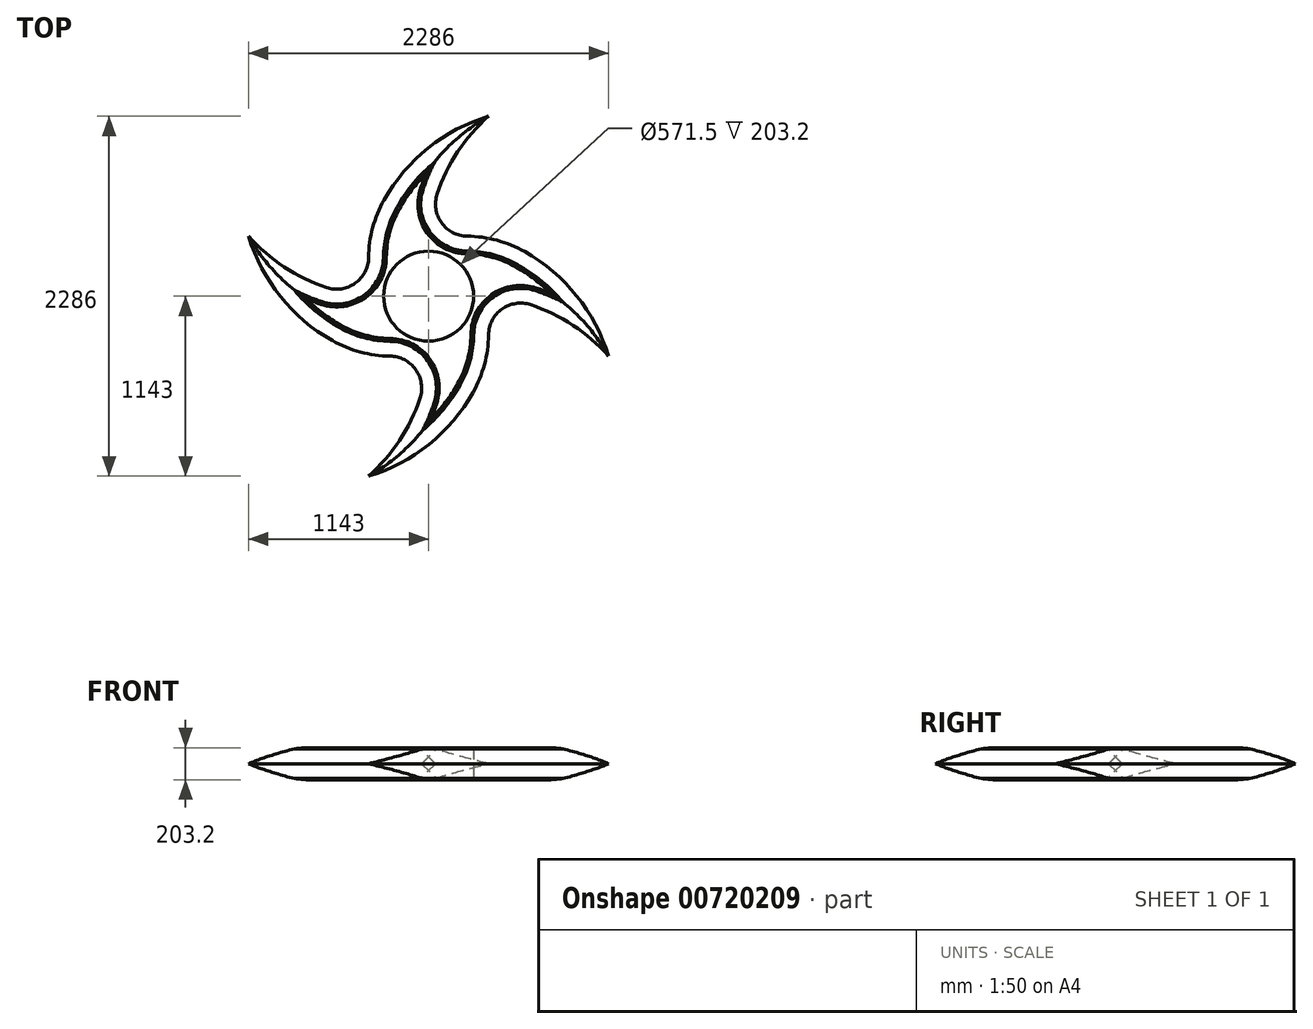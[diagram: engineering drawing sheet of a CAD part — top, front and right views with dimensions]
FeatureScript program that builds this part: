
annotation { "Feature Type Name" : "Feature", "Feature Type Description" : "" }
export const myFeature = defineFeature(function(context is Context, id is Id, definition is map)
    precondition{}
    {
        {
            var Q0;
            Q0=qCreatedBy(makeId("Top.planeOp"),FACE);
            var sketch = newSketch(context, id + "F0", { "sketchPlane" : qUnion([Q0])});
            skCircle(sketch, "E0", {"center": v(0, 0) * mm, "radius": 292.1 * mm});
            skCircle(sketch, "E1", {"center": v(0, 0) * mm, "radius": 381 * mm});
            skLineSegment(sketch, "E2", {"start": v(0, 0) * mm, "end": v(0, 381) * mm});
            skLineSegment(sketch, "E3", {"start": v(0, 381) * mm, "end": v(-381, 381) * mm});
            skLineSegment(sketch, "E4", {"start": v(-381, 381) * mm, "end": v(-381, -381) * mm});
            skLineSegment(sketch, "E5", {"start": v(-381, -381) * mm, "end": v(381, -381) * mm});
            skLineSegment(sketch, "E6", {"start": v(381, -381) * mm, "end": v(381, 381) * mm});
            skLineSegment(sketch, "E7", {"start": v(381, 381) * mm, "end": v(0, 381) * mm});
            skArc(sketch, "E8", {"start": v(381, 1143) * mm, "mid": v(-95.44, 857.44) * mm, "end": v(-381, 381) * mm});
            skArc(sketch, "E9", {"start": v(381, 1143) * mm, "mid": v(116.85, 798.82) * mm, "end": v(0, 381) * mm});
            skArc(sketch, "E10", {"start": v(-1143, 381) * mm, "mid": v(-857.44, -95.44) * mm, "end": v(-381, -381) * mm});
            skArc(sketch, "E11", {"start": v(-1143, 381) * mm, "mid": v(-798.82, 116.85) * mm, "end": v(-381, 0) * mm});
            skArc(sketch, "E12", {"start": v(-381, -1143) * mm, "mid": v(95.44, -857.44) * mm, "end": v(381, -381) * mm});
            skArc(sketch, "E13", {"start": v(-381, -1143) * mm, "mid": v(-116.85, -798.82) * mm, "end": v(0, -381) * mm});
            skArc(sketch, "E14", {"start": v(1143, -381) * mm, "mid": v(857.44, 95.44) * mm, "end": v(381, 381) * mm});
            skArc(sketch, "E15", {"start": v(1143, -381) * mm, "mid": v(798.82, -116.85) * mm, "end": v(381, 0) * mm});
            skCircle(sketch, "E16", {"center": v(0, 0) * mm, "radius": 285.75 * mm});
            skSolve(sketch);
        }
        {
            var Q0;
            {var subQ0=sQuery(id+"F0.wireOp",EDGE,"E12");Q0=makeQuery(id+"F0.imprint","IMPRINT",FACE,{"disambiguationData":[TD([[makeQuery(id+"F0.imprint","IMPRINT",EDGE,{"derivedFrom":subQ0}),1.0]])]});}
            var Q1;
            {var subQ0=sQuery(id+"F0.wireOp",EDGE,"E10");Q1=makeQuery(id+"F0.imprint","IMPRINT",FACE,{"disambiguationData":[TD([[makeQuery(id+"F0.imprint","IMPRINT",EDGE,{"derivedFrom":subQ0}),1.0]])]});}
            var Q2;
            Q2=makeQuery(id+"F0.imprint","IMPRINT",FACE,{"disambiguationData":[TD([[makeQuery(id+"F0.imprint","IMPRINT",EDGE,{"derivedFrom":sQuery(id+"F0.wireOp",EDGE,"E3")}),-1.0]])]});
            var Q3;
            {var subQ0=sQuery(id+"F0.wireOp",EDGE,"E14");Q3=makeQuery(id+"F0.imprint","IMPRINT",FACE,{"disambiguationData":[TD([[makeQuery(id+"F0.imprint","IMPRINT",EDGE,{"derivedFrom":subQ0}),1.0]])]});}
            var Q4;
            {var subQ0=sQuery(id+"F0.wireOp",EDGE,"E7");Q4=makeQuery(id+"F0.imprint","IMPRINT",FACE,{"disambiguationData":[TD([[makeQuery(id+"F0.imprint","IMPRINT",EDGE,{"derivedFrom":subQ0}),1.0]])]});}
            var Q5;
            {var subQ0=sQuery(id+"F0.wireOp",EDGE,"E3");Q5=makeQuery(id+"F0.imprint","IMPRINT",FACE,{"disambiguationData":[TD([[makeQuery(id+"F0.imprint","IMPRINT",EDGE,{"derivedFrom":subQ0}),1.0]])]});}
            var Q6;
            Q6=makeQuery(id+"F0.imprint","IMPRINT",FACE,{"disambiguationData":[TD([[makeQuery(id+"F0.imprint","IMPRINT",EDGE,{"derivedFrom":sQuery(id+"F0.wireOp",EDGE,"E0")}),-1.0]])]});
            var Q7;
            {var subQ0=sQuery(id+"F0.wireOp",EDGE,"E4");var subQ1=sQuery(id+"F0.wireOp",EDGE,"E1");var subQ2=makeQuery(id+"F0.imprint","INTERSECT",VERTEX,{"derivedFrom":[subQ1,subQ0,sQuery(id+"F0.wireOp",EDGE,"E11")]});Q7=makeQuery(id+"F0.imprint","IMPRINT",FACE,{"disambiguationData":[TD([[makeQuery(id+"F0.imprint","IMPRINT",EDGE,{"disambiguationData":[TD([[subQ2,-1.0]])],"derivedFrom":subQ1}),-1.0]])]});}
            var Q8;
            {var subQ0=sQuery(id+"F0.wireOp",EDGE,"E5");var subQ1=sQuery(id+"F0.wireOp",EDGE,"E1");var subQ2=makeQuery(id+"F0.imprint","INTERSECT",VERTEX,{"derivedFrom":[subQ1,subQ0,sQuery(id+"F0.wireOp",EDGE,"E13")]});Q8=makeQuery(id+"F0.imprint","IMPRINT",FACE,{"disambiguationData":[TD([[makeQuery(id+"F0.imprint","IMPRINT",EDGE,{"disambiguationData":[TD([[subQ2,-1.0]])],"derivedFrom":subQ1}),-1.0]])]});}
            var Q9;
            Q9=makeQuery(id+"F0.imprint","IMPRINT",FACE,{"disambiguationData":[TD([[makeQuery(id+"F0.imprint","IMPRINT",EDGE,{"derivedFrom":sQuery(id+"F0.wireOp",EDGE,"E0")}),1.0]])]});
            extrude(context, id + "F1", {"entities" : qUnion([Q0, Q1, Q2, Q3, Q4, Q5, Q6, Q7, Q8, Q9]), "depth" : 203.2 * mm, "offsetDistance" : 25.4 * mm});
        }
        {
            var Q0;
            Q0=makeQuery(id+"F1.opExtrude","SWEPT_EDGE",EDGE,{"disambiguationData":[OSD([sQuery(id+"F0.wireOp",EDGE,"E6"),sQuery(id+"F0.wireOp",EDGE,"E7"),sQuery(id+"F0.wireOp",EDGE,"E14")])]});
            var Q1;
            Q1=makeQuery(id+"F1.opExtrude","SWEPT_EDGE",EDGE,{"disambiguationData":[OSD([sQuery(id+"F0.wireOp",EDGE,"E3"),sQuery(id+"F0.wireOp",EDGE,"E4"),sQuery(id+"F0.wireOp",EDGE,"E8")])]});
            var Q2;
            Q2=makeQuery(id+"F1.opExtrude","SWEPT_EDGE",EDGE,{"disambiguationData":[OSD([sQuery(id+"F0.wireOp",EDGE,"E4"),sQuery(id+"F0.wireOp",EDGE,"E5"),sQuery(id+"F0.wireOp",EDGE,"E10")])]});
            var Q3;
            Q3=makeQuery(id+"F1.opExtrude","SWEPT_EDGE",EDGE,{"disambiguationData":[OSD([sQuery(id+"F0.wireOp",EDGE,"E5"),sQuery(id+"F0.wireOp",EDGE,"E6"),sQuery(id+"F0.wireOp",EDGE,"E12")])]});
            fillet(context, id + "F2", {"entities" : qUnion([Q0, Q1, Q2, Q3]), "radius" : 762 * mm, "tangentPropagation" : true, "allowEdgeOverflow" : false});
        }
        {
            var Q0;
            Q0=makeQuery(id+"F1.opExtrude","SWEPT_EDGE",EDGE,{"disambiguationData":[OSD([sQuery(id+"F0.wireOp",EDGE,"E1"),sQuery(id+"F0.wireOp",EDGE,"E4"),sQuery(id+"F0.wireOp",EDGE,"E11")])]});
            var Q1;
            Q1=makeQuery(id+"F1.opExtrude","SWEPT_EDGE",EDGE,{"disambiguationData":[OSD([sQuery(id+"F0.wireOp",EDGE,"E1"),sQuery(id+"F0.wireOp",EDGE,"E5"),sQuery(id+"F0.wireOp",EDGE,"E13")])]});
            var Q2;
            Q2=makeQuery(id+"F1.opExtrude","SWEPT_EDGE",EDGE,{"disambiguationData":[OSD([sQuery(id+"F0.wireOp",EDGE,"E1"),sQuery(id+"F0.wireOp",EDGE,"E6"),sQuery(id+"F0.wireOp",EDGE,"E15")])]});
            var Q3;
            Q3=makeQuery(id+"F1.opExtrude","SWEPT_EDGE",EDGE,{"disambiguationData":[OSD([sQuery(id+"F0.wireOp",EDGE,"E1"),sQuery(id+"F0.wireOp",EDGE,"E3"),sQuery(id+"F0.wireOp",EDGE,"E7"),sQuery(id+"F0.wireOp",EDGE,"E9")])]});
            fillet(context, id + "F3", {"entities" : qUnion([Q0, Q1, Q2, Q3]), "radius" : 203.2 * mm, "tangentPropagation" : true, "allowEdgeOverflow" : false});
        }
        {
            var Q0;
            Q0=makeQuery(id+"F1.opExtrude","CAP_EDGE",EDGE,{"disambiguationData":[OSD([sQuery(id+"F0.wireOp",EDGE,"E9")])],"isStart":false});
            var Q1;
            Q1=makeQuery(id+"F1.opExtrude","CAP_EDGE",EDGE,{"disambiguationData":[OSD([sQuery(id+"F0.wireOp",EDGE,"E9")])],"isStart":true});
            var Q2;
            Q2=makeQuery(id+"F1.opExtrude","CAP_EDGE",EDGE,{"disambiguationData":[OSD([sQuery(id+"F0.wireOp",EDGE,"E13")])],"isStart":true});
            var Q3;
            Q3=makeQuery(id+"F1.opExtrude","CAP_EDGE",EDGE,{"disambiguationData":[OSD([sQuery(id+"F0.wireOp",EDGE,"E13")])],"isStart":false});
            var Q4;
            Q4=makeQuery(id+"F1.opExtrude","CAP_EDGE",EDGE,{"disambiguationData":[OSD([sQuery(id+"F0.wireOp",EDGE,"E11")])],"isStart":false});
            var Q5;
            Q5=makeQuery(id+"F1.opExtrude","CAP_EDGE",EDGE,{"disambiguationData":[OSD([sQuery(id+"F0.wireOp",EDGE,"E11")])],"isStart":true});
            var Q6;
            {var subQ0=sQuery(id+"F0.wireOp",EDGE,"E15");var subQ1=sQuery(id+"F0.wireOp",EDGE,"E6");Q6=makeQuery(id+"F3.opFillet","BLEND_EDGE",EDGE,{"blendedFrom":[makeQuery(id+"F1.opExtrude","SWEPT_EDGE",EDGE,{"disambiguationData":[OSD([sQuery(id+"F0.wireOp",EDGE,"E1"),subQ1,subQ0])]}),makeQuery(id+"F1.opExtrude","CAP_FACE",FACE,{"disambiguationData":[OSD([sQuery(id+"F0.wireOp",EDGE,"E0"),sQuery(id+"F0.wireOp",EDGE,"E4"),sQuery(id+"F0.wireOp",EDGE,"E5"),subQ1,sQuery(id+"F0.wireOp",EDGE,"E7"),sQuery(id+"F0.wireOp",EDGE,"E8"),sQuery(id+"F0.wireOp",EDGE,"E9"),sQuery(id+"F0.wireOp",EDGE,"E10"),sQuery(id+"F0.wireOp",EDGE,"E11"),sQuery(id+"F0.wireOp",EDGE,"E12"),sQuery(id+"F0.wireOp",EDGE,"E13"),sQuery(id+"F0.wireOp",EDGE,"E14"),subQ0])],"isStart":false})],"blendedInto":[makeQuery(id+"F1.opExtrude","CAP_FACE",FACE,{"disambiguationData":[OSD([sQuery(id+"F0.wireOp",EDGE,"E0"),sQuery(id+"F0.wireOp",EDGE,"E4"),sQuery(id+"F0.wireOp",EDGE,"E5"),subQ1,sQuery(id+"F0.wireOp",EDGE,"E7"),sQuery(id+"F0.wireOp",EDGE,"E8"),sQuery(id+"F0.wireOp",EDGE,"E9"),sQuery(id+"F0.wireOp",EDGE,"E10"),sQuery(id+"F0.wireOp",EDGE,"E11"),sQuery(id+"F0.wireOp",EDGE,"E12"),sQuery(id+"F0.wireOp",EDGE,"E13"),sQuery(id+"F0.wireOp",EDGE,"E14"),subQ0])],"isStart":false})]});}
            var Q7;
            {var subQ0=sQuery(id+"F0.wireOp",EDGE,"E15");var subQ1=sQuery(id+"F0.wireOp",EDGE,"E6");Q7=makeQuery(id+"F3.opFillet","BLEND_EDGE",EDGE,{"blendedFrom":[makeQuery(id+"F1.opExtrude","SWEPT_EDGE",EDGE,{"disambiguationData":[OSD([sQuery(id+"F0.wireOp",EDGE,"E1"),subQ1,subQ0])]}),makeQuery(id+"F1.opExtrude","CAP_FACE",FACE,{"disambiguationData":[OSD([sQuery(id+"F0.wireOp",EDGE,"E0"),sQuery(id+"F0.wireOp",EDGE,"E4"),sQuery(id+"F0.wireOp",EDGE,"E5"),subQ1,sQuery(id+"F0.wireOp",EDGE,"E7"),sQuery(id+"F0.wireOp",EDGE,"E8"),sQuery(id+"F0.wireOp",EDGE,"E9"),sQuery(id+"F0.wireOp",EDGE,"E10"),sQuery(id+"F0.wireOp",EDGE,"E11"),sQuery(id+"F0.wireOp",EDGE,"E12"),sQuery(id+"F0.wireOp",EDGE,"E13"),sQuery(id+"F0.wireOp",EDGE,"E14"),subQ0])],"isStart":true})],"blendedInto":[makeQuery(id+"F1.opExtrude","CAP_FACE",FACE,{"disambiguationData":[OSD([sQuery(id+"F0.wireOp",EDGE,"E0"),sQuery(id+"F0.wireOp",EDGE,"E4"),sQuery(id+"F0.wireOp",EDGE,"E5"),subQ1,sQuery(id+"F0.wireOp",EDGE,"E7"),sQuery(id+"F0.wireOp",EDGE,"E8"),sQuery(id+"F0.wireOp",EDGE,"E9"),sQuery(id+"F0.wireOp",EDGE,"E10"),sQuery(id+"F0.wireOp",EDGE,"E11"),sQuery(id+"F0.wireOp",EDGE,"E12"),sQuery(id+"F0.wireOp",EDGE,"E13"),sQuery(id+"F0.wireOp",EDGE,"E14"),subQ0])],"isStart":true})]});}
            chamfer(context, id + "F4", {"entities" : qUnion([Q0, Q1, Q2, Q3, Q4, Q5, Q6, Q7]), "width" : 101.6 * mm, "tangentPropagation" : true});
        }
        {
            var Q0;
            {var subQ0=sQuery(id+"F0.wireOp",EDGE,"E15");var subQ1=sQuery(id+"F0.wireOp",EDGE,"E6");var subQ2=makeQuery(id+"F1.opExtrude","CAP_FACE",FACE,{"disambiguationData":[OSD([sQuery(id+"F0.wireOp",EDGE,"E0"),sQuery(id+"F0.wireOp",EDGE,"E4"),sQuery(id+"F0.wireOp",EDGE,"E5"),subQ1,sQuery(id+"F0.wireOp",EDGE,"E7"),sQuery(id+"F0.wireOp",EDGE,"E8"),sQuery(id+"F0.wireOp",EDGE,"E9"),sQuery(id+"F0.wireOp",EDGE,"E10"),sQuery(id+"F0.wireOp",EDGE,"E11"),sQuery(id+"F0.wireOp",EDGE,"E12"),sQuery(id+"F0.wireOp",EDGE,"E13"),sQuery(id+"F0.wireOp",EDGE,"E14"),subQ0])],"isStart":false});Q0=makeQuery(id+"F4.opChamfer","BLEND_EDGE",EDGE,{"blendedFrom":[makeQuery(id+"F3.opFillet","BLEND_EDGE",EDGE,{"blendedFrom":[makeQuery(id+"F1.opExtrude","SWEPT_EDGE",EDGE,{"disambiguationData":[OSD([sQuery(id+"F0.wireOp",EDGE,"E1"),subQ1,subQ0])]}),subQ2],"blendedInto":[subQ2]}),subQ2],"blendedInto":[subQ2]});}
            var Q1;
            {var subQ0=sQuery(id+"F0.wireOp",EDGE,"E14");var subQ1=sQuery(id+"F0.wireOp",EDGE,"E7");var subQ2=sQuery(id+"F0.wireOp",EDGE,"E6");var subQ3=makeQuery(id+"F1.opExtrude","CAP_FACE",FACE,{"disambiguationData":[OSD([sQuery(id+"F0.wireOp",EDGE,"E0"),sQuery(id+"F0.wireOp",EDGE,"E4"),sQuery(id+"F0.wireOp",EDGE,"E5"),subQ2,subQ1,sQuery(id+"F0.wireOp",EDGE,"E8"),sQuery(id+"F0.wireOp",EDGE,"E9"),sQuery(id+"F0.wireOp",EDGE,"E10"),sQuery(id+"F0.wireOp",EDGE,"E11"),sQuery(id+"F0.wireOp",EDGE,"E12"),sQuery(id+"F0.wireOp",EDGE,"E13"),subQ0,sQuery(id+"F0.wireOp",EDGE,"E15")])],"isStart":false});Q1=makeQuery(id+"F4.opChamfer","BLEND_EDGE",EDGE,{"blendedFrom":[makeQuery(id+"F2.opFillet","BLEND_EDGE",EDGE,{"blendedFrom":[makeQuery(id+"F1.opExtrude","SWEPT_EDGE",EDGE,{"disambiguationData":[OSD([subQ2,subQ1,subQ0])]}),subQ3],"blendedInto":[subQ3]}),subQ3],"blendedInto":[subQ3]});}
            var Q2;
            {var subQ0=sQuery(id+"F0.wireOp",EDGE,"E13");var subQ1=sQuery(id+"F0.wireOp",EDGE,"E5");var subQ2=makeQuery(id+"F1.opExtrude","CAP_FACE",FACE,{"disambiguationData":[OSD([sQuery(id+"F0.wireOp",EDGE,"E0"),sQuery(id+"F0.wireOp",EDGE,"E4"),subQ1,sQuery(id+"F0.wireOp",EDGE,"E6"),sQuery(id+"F0.wireOp",EDGE,"E7"),sQuery(id+"F0.wireOp",EDGE,"E8"),sQuery(id+"F0.wireOp",EDGE,"E9"),sQuery(id+"F0.wireOp",EDGE,"E10"),sQuery(id+"F0.wireOp",EDGE,"E11"),sQuery(id+"F0.wireOp",EDGE,"E12"),subQ0,sQuery(id+"F0.wireOp",EDGE,"E14"),sQuery(id+"F0.wireOp",EDGE,"E15")])],"isStart":false});Q2=makeQuery(id+"F4.opChamfer","BLEND_EDGE",EDGE,{"blendedFrom":[makeQuery(id+"F3.opFillet","BLEND_EDGE",EDGE,{"blendedFrom":[makeQuery(id+"F1.opExtrude","SWEPT_EDGE",EDGE,{"disambiguationData":[OSD([sQuery(id+"F0.wireOp",EDGE,"E1"),subQ1,subQ0])]}),subQ2],"blendedInto":[subQ2]}),subQ2],"blendedInto":[subQ2]});}
            var Q3;
            {var subQ0=sQuery(id+"F0.wireOp",EDGE,"E11");var subQ1=sQuery(id+"F0.wireOp",EDGE,"E4");var subQ2=makeQuery(id+"F1.opExtrude","CAP_FACE",FACE,{"disambiguationData":[OSD([sQuery(id+"F0.wireOp",EDGE,"E0"),subQ1,sQuery(id+"F0.wireOp",EDGE,"E5"),sQuery(id+"F0.wireOp",EDGE,"E6"),sQuery(id+"F0.wireOp",EDGE,"E7"),sQuery(id+"F0.wireOp",EDGE,"E8"),sQuery(id+"F0.wireOp",EDGE,"E9"),sQuery(id+"F0.wireOp",EDGE,"E10"),subQ0,sQuery(id+"F0.wireOp",EDGE,"E12"),sQuery(id+"F0.wireOp",EDGE,"E13"),sQuery(id+"F0.wireOp",EDGE,"E14"),sQuery(id+"F0.wireOp",EDGE,"E15")])],"isStart":false});Q3=makeQuery(id+"F4.opChamfer","BLEND_EDGE",EDGE,{"blendedFrom":[makeQuery(id+"F3.opFillet","BLEND_EDGE",EDGE,{"blendedFrom":[makeQuery(id+"F1.opExtrude","SWEPT_EDGE",EDGE,{"disambiguationData":[OSD([sQuery(id+"F0.wireOp",EDGE,"E1"),subQ1,subQ0])]}),subQ2],"blendedInto":[subQ2]}),subQ2],"blendedInto":[subQ2]});}
            var Q4;
            {var subQ0=sQuery(id+"F0.wireOp",EDGE,"E11");var subQ1=sQuery(id+"F0.wireOp",EDGE,"E4");var subQ2=makeQuery(id+"F1.opExtrude","CAP_FACE",FACE,{"disambiguationData":[OSD([sQuery(id+"F0.wireOp",EDGE,"E0"),subQ1,sQuery(id+"F0.wireOp",EDGE,"E5"),sQuery(id+"F0.wireOp",EDGE,"E6"),sQuery(id+"F0.wireOp",EDGE,"E7"),sQuery(id+"F0.wireOp",EDGE,"E8"),sQuery(id+"F0.wireOp",EDGE,"E9"),sQuery(id+"F0.wireOp",EDGE,"E10"),subQ0,sQuery(id+"F0.wireOp",EDGE,"E12"),sQuery(id+"F0.wireOp",EDGE,"E13"),sQuery(id+"F0.wireOp",EDGE,"E14"),sQuery(id+"F0.wireOp",EDGE,"E15")])],"isStart":true});Q4=makeQuery(id+"F4.opChamfer","BLEND_EDGE",EDGE,{"blendedFrom":[makeQuery(id+"F3.opFillet","BLEND_EDGE",EDGE,{"blendedFrom":[makeQuery(id+"F1.opExtrude","SWEPT_EDGE",EDGE,{"disambiguationData":[OSD([sQuery(id+"F0.wireOp",EDGE,"E1"),subQ1,subQ0])]}),subQ2],"blendedInto":[subQ2]}),subQ2],"blendedInto":[subQ2]});}
            var Q5;
            {var subQ0=sQuery(id+"F0.wireOp",EDGE,"E10");var subQ1=sQuery(id+"F0.wireOp",EDGE,"E5");var subQ2=sQuery(id+"F0.wireOp",EDGE,"E4");var subQ3=makeQuery(id+"F1.opExtrude","CAP_FACE",FACE,{"disambiguationData":[OSD([sQuery(id+"F0.wireOp",EDGE,"E0"),subQ2,subQ1,sQuery(id+"F0.wireOp",EDGE,"E6"),sQuery(id+"F0.wireOp",EDGE,"E7"),sQuery(id+"F0.wireOp",EDGE,"E8"),sQuery(id+"F0.wireOp",EDGE,"E9"),subQ0,sQuery(id+"F0.wireOp",EDGE,"E11"),sQuery(id+"F0.wireOp",EDGE,"E12"),sQuery(id+"F0.wireOp",EDGE,"E13"),sQuery(id+"F0.wireOp",EDGE,"E14"),sQuery(id+"F0.wireOp",EDGE,"E15")])],"isStart":true});Q5=makeQuery(id+"F4.opChamfer","BLEND_EDGE",EDGE,{"blendedFrom":[makeQuery(id+"F2.opFillet","BLEND_EDGE",EDGE,{"blendedFrom":[makeQuery(id+"F1.opExtrude","SWEPT_EDGE",EDGE,{"disambiguationData":[OSD([subQ2,subQ1,subQ0])]}),subQ3],"blendedInto":[subQ3]}),subQ3],"blendedInto":[subQ3]});}
            var Q6;
            {var subQ0=sQuery(id+"F0.wireOp",EDGE,"E12");var subQ1=sQuery(id+"F0.wireOp",EDGE,"E6");var subQ2=sQuery(id+"F0.wireOp",EDGE,"E5");var subQ3=makeQuery(id+"F1.opExtrude","CAP_FACE",FACE,{"disambiguationData":[OSD([sQuery(id+"F0.wireOp",EDGE,"E0"),sQuery(id+"F0.wireOp",EDGE,"E4"),subQ2,subQ1,sQuery(id+"F0.wireOp",EDGE,"E7"),sQuery(id+"F0.wireOp",EDGE,"E8"),sQuery(id+"F0.wireOp",EDGE,"E9"),sQuery(id+"F0.wireOp",EDGE,"E10"),sQuery(id+"F0.wireOp",EDGE,"E11"),subQ0,sQuery(id+"F0.wireOp",EDGE,"E13"),sQuery(id+"F0.wireOp",EDGE,"E14"),sQuery(id+"F0.wireOp",EDGE,"E15")])],"isStart":true});Q6=makeQuery(id+"F4.opChamfer","BLEND_EDGE",EDGE,{"blendedFrom":[makeQuery(id+"F2.opFillet","BLEND_EDGE",EDGE,{"blendedFrom":[makeQuery(id+"F1.opExtrude","SWEPT_EDGE",EDGE,{"disambiguationData":[OSD([subQ2,subQ1,subQ0])]}),subQ3],"blendedInto":[subQ3]}),subQ3],"blendedInto":[subQ3]});}
            var Q7;
            {var subQ0=sQuery(id+"F0.wireOp",EDGE,"E9");var subQ1=sQuery(id+"F0.wireOp",EDGE,"E7");var subQ2=makeQuery(id+"F1.opExtrude","CAP_FACE",FACE,{"disambiguationData":[OSD([sQuery(id+"F0.wireOp",EDGE,"E0"),sQuery(id+"F0.wireOp",EDGE,"E4"),sQuery(id+"F0.wireOp",EDGE,"E5"),sQuery(id+"F0.wireOp",EDGE,"E6"),subQ1,sQuery(id+"F0.wireOp",EDGE,"E8"),subQ0,sQuery(id+"F0.wireOp",EDGE,"E10"),sQuery(id+"F0.wireOp",EDGE,"E11"),sQuery(id+"F0.wireOp",EDGE,"E12"),sQuery(id+"F0.wireOp",EDGE,"E13"),sQuery(id+"F0.wireOp",EDGE,"E14"),sQuery(id+"F0.wireOp",EDGE,"E15")])],"isStart":true});Q7=makeQuery(id+"F4.opChamfer","BLEND_EDGE",EDGE,{"blendedFrom":[makeQuery(id+"F3.opFillet","BLEND_EDGE",EDGE,{"blendedFrom":[makeQuery(id+"F1.opExtrude","SWEPT_EDGE",EDGE,{"disambiguationData":[OSD([sQuery(id+"F0.wireOp",EDGE,"E1"),sQuery(id+"F0.wireOp",EDGE,"E3"),subQ1,subQ0])]}),subQ2],"blendedInto":[subQ2]}),subQ2],"blendedInto":[subQ2]});}
            chamfer(context, id + "F5", {"entities" : qUnion([Q0, Q1, Q2, Q3, Q4, Q5, Q6, Q7]), "width" : 25.4 * mm, "tangentPropagation" : true});
        }
    });
